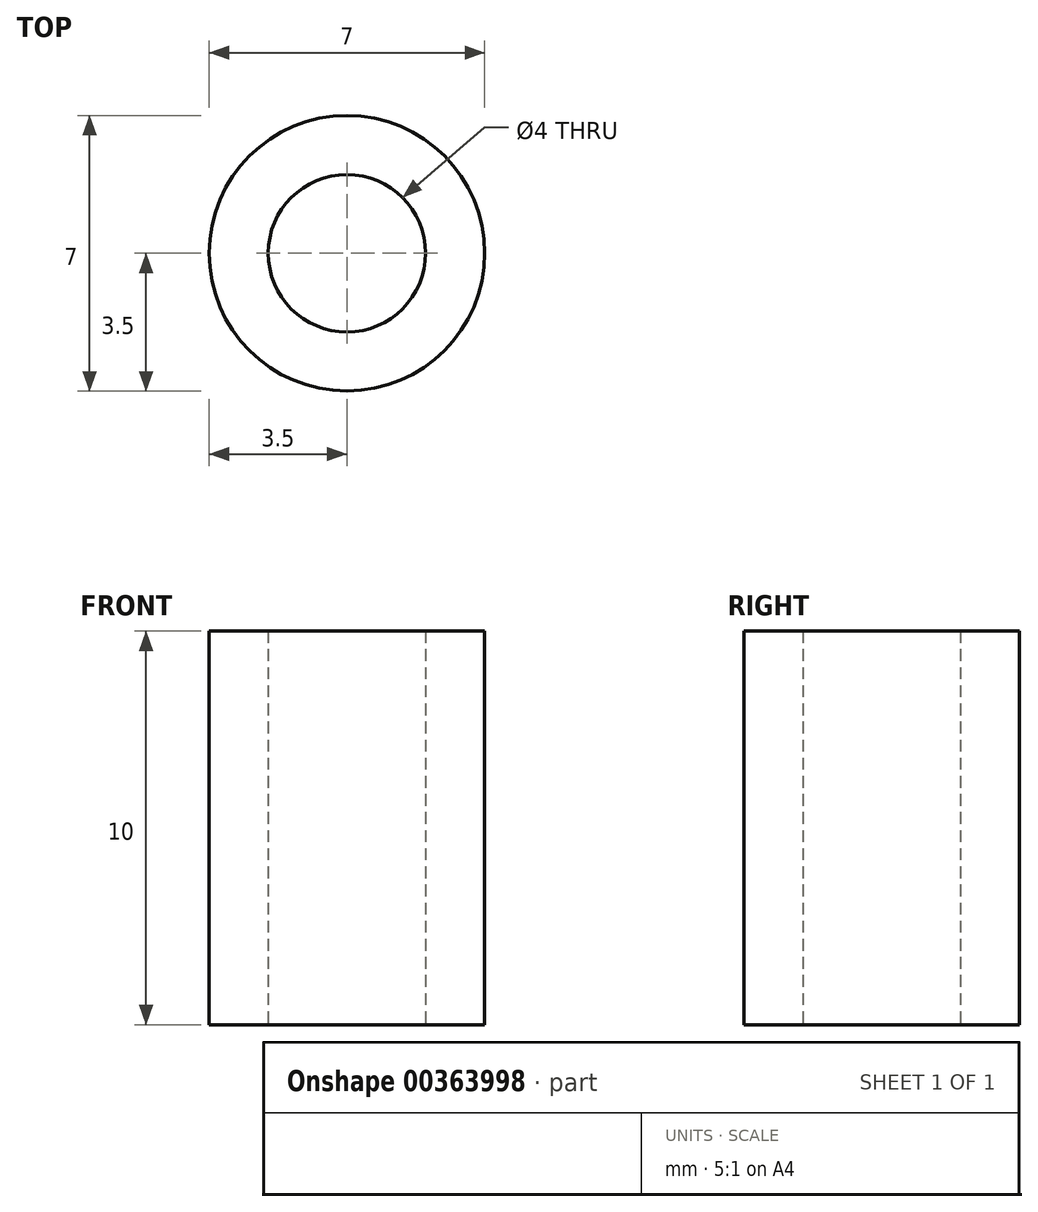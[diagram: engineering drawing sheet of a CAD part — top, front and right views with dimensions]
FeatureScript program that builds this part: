
annotation { "Feature Type Name" : "Feature", "Feature Type Description" : "" }
export const myFeature = defineFeature(function(context is Context, id is Id, definition is map)
    precondition{}
    {
        {
            var Q0;
            Q0=qCreatedBy(makeId("Top.planeOp"),FACE);
            var sketch = newSketch(context, id + "F0", { "sketchPlane" : qUnion([Q0])});
            skCircle(sketch, "E0", {"center": v(0, 0) * mm, "radius": 3.5 * mm});
            skCircle(sketch, "E1", {"center": v(0, 0) * mm, "radius": 2 * mm});
            skSolve(sketch);
        }
        {
            var Q0;
            Q0 = qSketchRegion(id + "F0", true);
            extrude(context, id + "F1", {"entities" : qUnion([Q0]), "depth" : 10 * mm, "offsetDistance" : 25 * mm});
        }
    });
